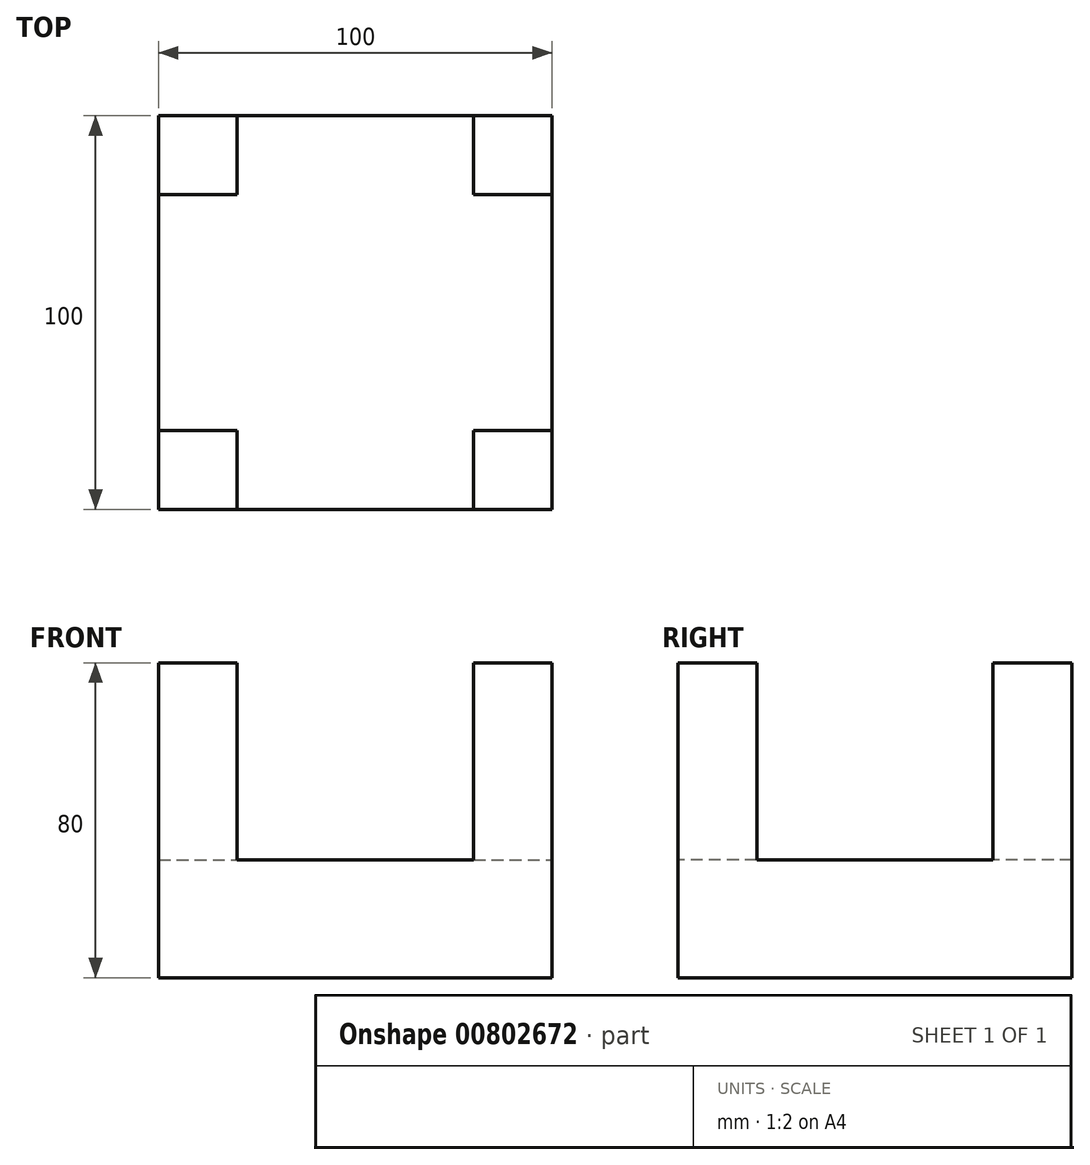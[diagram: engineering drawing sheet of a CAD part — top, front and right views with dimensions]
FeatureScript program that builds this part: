
annotation { "Feature Type Name" : "Feature", "Feature Type Description" : "" }
export const myFeature = defineFeature(function(context is Context, id is Id, definition is map)
    precondition{}
    {
        {
            var Q0;
            Q0=qCreatedBy(makeId("Top.planeOp"),FACE);
            var sketch = newSketch(context, id + "F0", { "sketchPlane" : qUnion([Q0])});
            skLineSegment(sketch, "E0.bottom", {"start": v(-64.13, 54.93) * mm, "end": v(35.87, 54.93) * mm});
            skLineSegment(sketch, "E0.top", {"start": v(-64.13, -45.07) * mm, "end": v(35.87, -45.07) * mm});
            skLineSegment(sketch, "E0.left", {"start": v(-64.13, 54.93) * mm, "end": v(-64.13, -45.07) * mm});
            skLineSegment(sketch, "E0.right", {"start": v(35.87, 54.93) * mm, "end": v(35.87, -45.07) * mm});
            skSolve(sketch);
        }
        {
            var Q0;
            Q0=makeQuery(id+"F0.imprint","IMPRINT",FACE,{"disambiguationData":[TD([[makeQuery(id+"F0.imprint","IMPRINT",EDGE,{"derivedFrom":sQuery(id+"F0.wireOp",EDGE,"E0.bottom")}),-1.0]])]});
            extrude(context, id + "F1", {"entities" : qUnion([Q0]), "depth" : 30 * mm, "offsetDistance" : 25 * mm});
        }
        {
            var Q0;
            Q0=makeQuery(id+"F1.opExtrude","CAP_FACE",FACE,{"disambiguationData":[OSD([sQuery(id+"F0.wireOp",EDGE,"E0.bottom"),sQuery(id+"F0.wireOp",EDGE,"E0.top"),sQuery(id+"F0.wireOp",EDGE,"E0.left"),sQuery(id+"F0.wireOp",EDGE,"E0.right")])],"isStart":false});
            var sketch = newSketch(context, id + "F2", { "sketchPlane" : qUnion([Q0])});
            skLineSegment(sketch, "E1.bottom", {"start": v(-64.13, -25.07) * mm, "end": v(-44.13, -25.07) * mm});
            skLineSegment(sketch, "E1.top", {"start": v(-64.13, -45.07) * mm, "end": v(-44.13, -45.07) * mm});
            skLineSegment(sketch, "E1.left", {"start": v(-64.13, -25.07) * mm, "end": v(-64.13, -45.07) * mm});
            skLineSegment(sketch, "E1.right", {"start": v(-44.13, -25.07) * mm, "end": v(-44.13, -45.07) * mm});
            skLineSegment(sketch, "E2.bottom", {"start": v(-64.13, 54.93) * mm, "end": v(-44.13, 54.93) * mm});
            skLineSegment(sketch, "E2.top", {"start": v(-64.13, 34.93) * mm, "end": v(-44.13, 34.93) * mm});
            skLineSegment(sketch, "E2.left", {"start": v(-64.13, 54.93) * mm, "end": v(-64.13, 34.93) * mm});
            skLineSegment(sketch, "E2.right", {"start": v(-44.13, 54.93) * mm, "end": v(-44.13, 34.93) * mm});
            skLineSegment(sketch, "E3.bottom", {"start": v(35.87, 54.93) * mm, "end": v(15.87, 54.93) * mm});
            skLineSegment(sketch, "E3.top", {"start": v(35.87, 34.93) * mm, "end": v(15.87, 34.93) * mm});
            skLineSegment(sketch, "E3.left", {"start": v(35.87, 54.93) * mm, "end": v(35.87, 34.93) * mm});
            skLineSegment(sketch, "E3.right", {"start": v(15.87, 54.93) * mm, "end": v(15.87, 34.93) * mm});
            skLineSegment(sketch, "E4.bottom", {"start": v(0, -25.07) * mm, "end": v(35.87, -25.07) * mm});
            skLineSegment(sketch, "E4.top", {"start": v(15.87, -45.07) * mm, "end": v(35.87, -45.07) * mm});
            skLineSegment(sketch, "E4.left", {"start": v(15.87, -25.07) * mm, "end": v(15.87, -45.07) * mm});
            skLineSegment(sketch, "E4.right", {"start": v(35.87, -25.07) * mm, "end": v(35.87, -45.07) * mm});
            skSolve(sketch);
        }
        {
            var Q0;
            Q0 = qSketchRegion(id + "F2", true);
            extrude(context, id + "F3", {"entities" : qUnion([Q0]), "operationType" : NewBodyOperationType.ADD, "depth" : 50 * mm, "offsetDistance" : 25 * mm});
        }
    });
